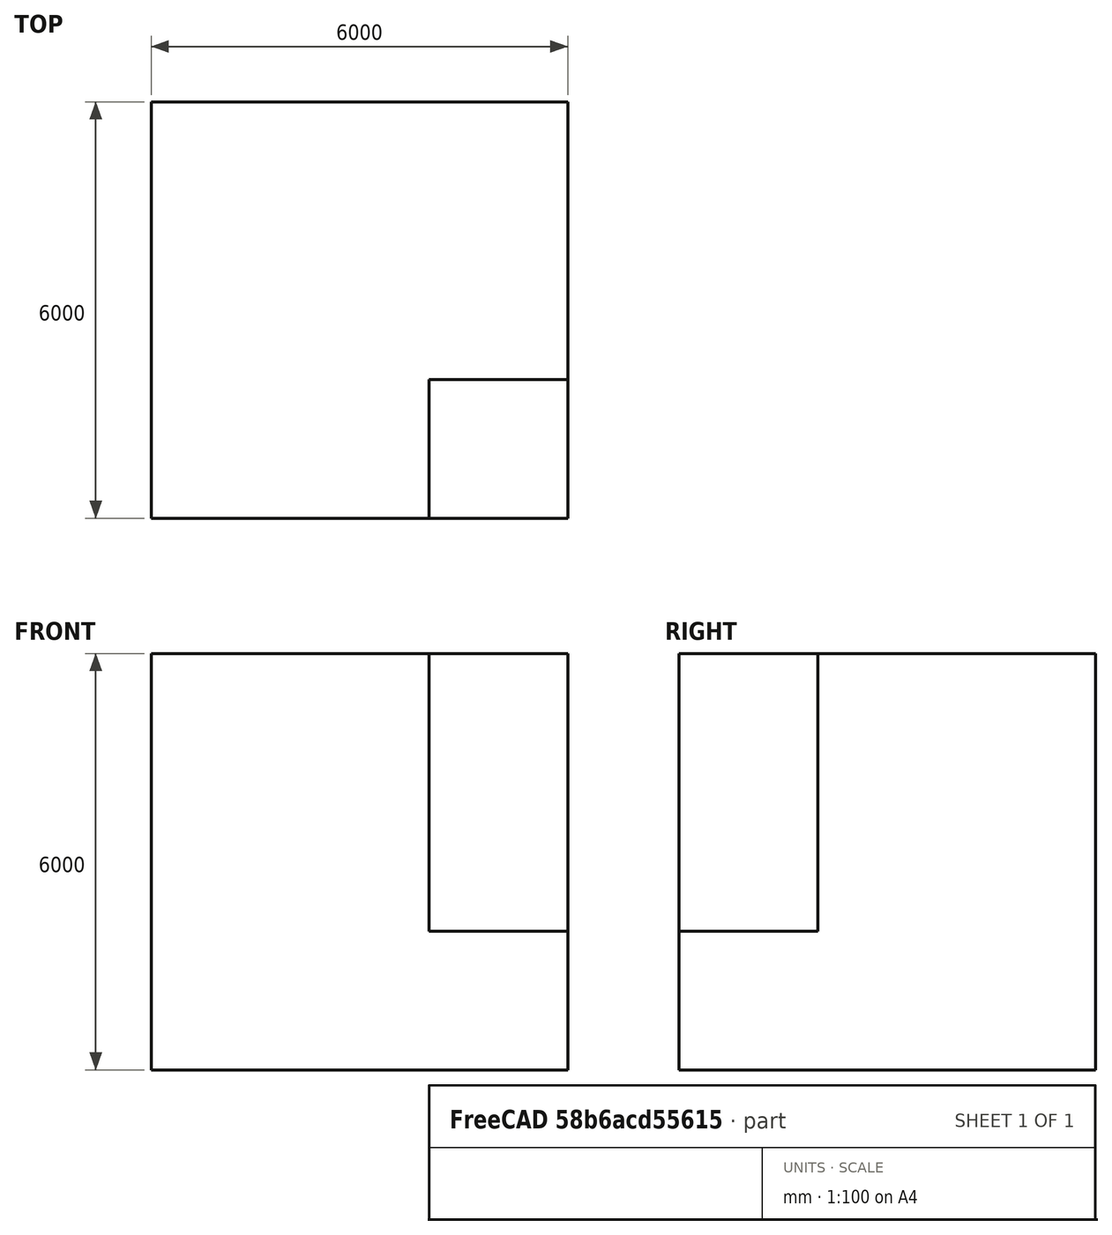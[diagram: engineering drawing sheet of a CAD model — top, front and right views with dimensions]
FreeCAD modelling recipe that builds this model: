
FCSTD DOCUMENT  (FreeCAD 0.21R33694 (Git))
Label: Pit_Example
License: All rights reserved
LicenseURL: http://en.wikipedia.org/wiki/All_rights_reserved
objects: Fem::ConstraintDisplacement×3, Part::Box×2, Fem::FemMeshObjectPython×2, Part::FeaturePython×1, App::MaterialObjectPython×1, Fem::FemSolverObjectPython×1, Fem::FemResultObjectPython×1, Fem::FemAnalysis×1
note: 3 computed .brp shape members not serialized (recipe doc carries the construction recipe); baked Part::Feature solids carry a one-line shape summary decoded from their .brp

FEATURE [Part::Box] Box  label="Cube"
  AttacherType = Attacher::AttachEngine3D
  Height = 6000
  Length = 6000
  Width = 6000
FEATURE [Part::Box] Box001  label="Cube001"
  AttacherType = Attacher::AttachEngine3D
  Height = 4000
  Length = 2000
  Placement = pos=(4000,0,2000) rot=(0,0,1;0rad)
  Width = 2000
FEATURE [Part::FeaturePython] XOR  # WARN: FeaturePython — macro-defined, semantics opaque (R4)
  Objects = -> [Box,Box001]
  Tolerance = 0
FEATURE [Fem::FemMeshObjectPython] FEMMeshGmsh  # FEM object (typed FeaturePython)
  Algorithm2D = 0
  Algorithm3D = 0
  CharacteristicLengthMax = 1000
  CharacteristicLengthMin = 1000
  CoherenceMesh = true
  ElementDimension = 0
  ElementOrder = 1
  GeometryTolerance = 1e-06
  GroupsOfNodes = false
  HighOrderOptimize = 0
  MeshSizeFromCurvature = 12
  OptimizeNetgen = false
  OptimizeStd = true
  Part = -> XOR
  RecombinationAlgorithm = 0
  Recombine3DAll = false
  RecombineAll = false
  SecondOrderLinear = false
FEATURE [Fem::ConstraintDisplacement] FemConstraintDisplacement
  NormalDirection = (0,-1,0)
  Normals = (82) [(0,-1,0),(0,-1,0),(0,-1,0),(0,-1,0),(0,-1,0),(0,-1,0),(0,-1,0),(0,-1,0),(0,-1,0),(0,-1,0),(0,-1,0),(0,-1,0),(0,-1,0),(0,-1,0),(0,-1,0),(0,-1,0),+66 more]
  Points = (82) [(0,0,0),(0,0,666.667),(0,0,1333.33),(0,0,2000),(0,0,2666.67),(0,0,3333.33),(0,0,4000),(0,0,4666.67),(0,0,5333.33),(0,0,6000),(666.667,0,0),+71 more]
  References = -> [XOR]
  Scale = 66
  hasXFormula = false
  hasYFormula = false
  hasZFormula = false
  rotxFix = false
  rotxFree = true
  rotyFix = false
  rotyFree = true
  rotzFix = false
  rotzFree = true
  useFlowSurfaceForce = false
  xDisplacement = 0
  xFix = false
  xFree = true
  xRotation = 0
  yDisplacement = 0
  yFix = true
  yFree = false
  yRotation = 0
  zDisplacement = 0
  zFix = false
  zFree = true
  zRotation = 0
FEATURE [Fem::ConstraintDisplacement] FemConstraintDisplacement001
  NormalDirection = (1,0,0)
  Normals = (82) [(1,0,0),(1,0,0),(1,0,0),(1,0,0),(1,0,0),(1,0,0),(1,0,0),(1,0,0),(1,0,0),(1,0,0),(1,0,0),(1,0,0),(1,0,0),(1,0,0),(1,0,0),(1,0,0),(1,0,0),(1,0,0),+64 more]
  Points = (82) [(6000,6000,0),(6000,6000,666.667),(6000,6000,1333.33),(6000,6000,2000),(6000,6000,2666.67),(6000,6000,3333.33),(6000,6000,4000),(6000,6000,4666.67),+74 more]
  References = -> [XOR]
  Scale = 66
  hasXFormula = false
  hasYFormula = false
  hasZFormula = false
  rotxFix = false
  rotxFree = true
  rotyFix = false
  rotyFree = true
  rotzFix = false
  rotzFree = true
  useFlowSurfaceForce = false
  xDisplacement = 0
  xFix = true
  xFree = false
  xRotation = 0
  yDisplacement = 0
  yFix = false
  yFree = true
  yRotation = 0
  zDisplacement = 0
  zFix = false
  zFree = true
  zRotation = 0
FEATURE [Fem::ConstraintDisplacement] FemConstraintDisplacement002
  NormalDirection = (-1,0,0)
  Normals = (300) [(-1,0,0),(-1,0,0),(-1,0,0),(-1,0,0),(-1,0,0),(-1,0,0),(-1,0,0),(-1,0,0),(-1,0,0),(-1,0,0),(-1,0,0),(-1,0,0),(-1,0,0),(-1,0,0),(-1,0,0),(-1,0,0),+284 more]
  Points = (300) [(0,6000,0),(0,6000,666.667),(0,6000,1333.33),(0,6000,2000),(0,6000,2666.67),(0,6000,3333.33),(0,6000,4000),(0,6000,4666.67),(0,6000,5333.33),+291 more]
  References = -> [XOR]
  Scale = 66
  hasXFormula = false
  hasYFormula = false
  hasZFormula = false
  rotxFix = false
  rotxFree = true
  rotyFix = false
  rotyFree = true
  rotzFix = false
  rotzFree = true
  useFlowSurfaceForce = false
  xDisplacement = 0
  xFix = true
  xFree = false
  xRotation = 0
  yDisplacement = 0
  yFix = true
  yFree = false
  yRotation = 0
  zDisplacement = 0
  zFix = true
  zFree = false
  zRotation = 0
FEATURE [App::MaterialObjectPython] SolidMaterial  # material (typed FeaturePython)
  Category = 0
  Material = Density=2000 kg/m^3,Description=Standard steel material for CalculiX sample calculations,Father=Metal,Name=CalculiX-Steel,PoissonRatio=0.3,+4 more (map truncated)
FEATURE [Fem::FemSolverObjectPython] SolverCcxTools  # FEM object (typed FeaturePython)
  AnalysisType = 0
  BeamShellResultOutput3D = false
  BucklingFactors = 1
  EigenmodeHighLimit = 1000000
  EigenmodeLowLimit = 0
  EigenmodesCount = 10
  GeometricalNonlinearity = 0
  IterationsControlParameterCutb = 0.25,0.5,0.75,0.85,,,1.5,
  IterationsControlParameterIter = 4,8,9,200,10,400,,200,,
  IterationsControlParameterTimeUse = false
  IterationsThermoMechMaximum = 2000
  IterationsUserDefinedIncrementations = false
  IterationsUserDefinedTimeStepLength = false
  MaterialNonlinearity = 0
  MatrixSolverType = 0
  SplitInputWriter = false
  ThermoMechSteadyState = true
  TimeEnd = 1
  TimeInitialStep = 0.01
FEATURE [Fem::FemMeshObjectPython] Result_Mesh_Volume  # FEM object (typed FeaturePython)
FEATURE [Fem::FemResultObjectPython] ResultMechanical  # FEM object (typed FeaturePython)
  CriticalStrainRatio = [3.93271e-11,3.65733e-15,3.60697e-13,0,1.03974e-16,0,5.69735e-13,0,2.90723e-11,0,4.77787e-14,3.35108e-15,3.15501e-13,5.30155e-13,1.25867e-14,3.70262e-14,9.67589e-14,1.55294e-13,4.09489e-13,6.47917e-15,2.40662e-14,5.35308e-14,1.18882e-13,+2136 more]
  DisplacementLengths = [0,0,0,0,0,13.4161,499.853,1214.43,0,1229.44,1042.92,0,395.681,315.697,0,0,0,0,0,0,0,0,0,0,0,0,0,0,0,0,0,0,0,0,0,0,0,0,0,0,0,0,0,0,0,0,0,0,0,0,0,0,0,0,0,0,0,0,26.8115,21.3072,22.4792,44.2649,244.595,20.9739,1203.36,1133.48,1185.39,1077,+2091 more]
  DisplacementVectors = (2159) [(0,0,0),(0,0,0),(0,0,0),(0,0,0),(0,0,0),(0,0,-13.4161),(471.161,0,-166.914),(359.54,0,-1159.99),(0,0,0),(0,-364.791,-1174.08),+2149 more]
  Eigenmode = 0
  EigenmodeFrequency = 0
  MaxShear = [0.0120873,0.00838715,0.00834008,0.00200348,0.0119649,0.0107051,0.0124848,0.00878505,0.0122617,0.00891737,0.00945304,0.0083381,0.0122458,0.0106498,0.0122897,0.0124146,0.0123189,0.0117055,0.0119133,0.0123287,0.0116299,0.0122706,0.0117304,+2136 more]
  Mesh = -> Result_Mesh_Volume
  NodeNumbers = [1,2,3,4,5,6,7,8,9,10,11,12,13,14,15,16,17,18,19,20,21,22,23,24,25,26,27,28,29,30,31,32,33,34,35,36,37,38,39,40,41,42,43,44,45,46,47,48,49,50,51,52,53,54,55,56,57,58,59,60,61,62,63,64,65,66,67,68,69,+2090 more]
  NodeStressXX = [0.0426116,-0.0287495,0.0225941,0.000184001,-0.0236186,-0.0213899,-0.0258921,-0.000334487,0.0374222,-0.0176534,-0.0194084,-0.0200504,-0.0263269,-0.0342568,-0.0468423,-0.0339447,-0.0240208,-0.0144466,-0.00358832,-0.0455244,-0.0404945,+2138 more]
  NodeStressXY = [0.000436366,0.00123217,-0.00346757,0.00119999,-0.000608948,0.000394579,-0.00115889,0.000984407,0.000109046,0.000807043,-0.00663616,0.00119992,-0.000516293,-0.00632209,4.25731e-05,-4.16024e-05,-7.06763e-06,-1.05395e-06,-1.28247e-05,+2140 more]
  NodeStressXZ = [-0.0114819,-0.00827964,-0.00392951,-0.0013586,0.00153304,8.95455e-05,0.0118325,0.000849509,-0.000294895,0.000139663,1.71635e-05,-0.00121717,-0.0016558,0.00682086,-0.0110895,-0.0121039,-0.0121837,-0.0116967,-0.0118399,-0.0101755,-0.0110692,+2138 more]
  NodeStressYY = [0.0416871,-0.0204887,0.0222457,9.08532e-05,-0.0239155,-0.0208947,-0.0282729,-0.0170663,0.0379403,-0.000990802,-0.0198669,-0.0277336,-0.0258271,-0.0339999,-0.0380442,-0.0296529,-0.0212854,-0.0135228,-0.0012541,-0.0331274,-0.0339659,+2138 more]
  NodeStressYZ = [0.000121712,0.00118817,0.00397418,0.00141301,-0.0015193,-0.000209556,0.00261372,-0.00023663,0.0118684,-0.00119348,1.03204e-06,0.00821444,-0.012117,-0.00570276,-5.44293e-05,-0.000192069,-9.10624e-05,3.38103e-06,3.55138e-05,-7.92996e-05,+2139 more]
  NodeStressZZ = [0.0351114,-0.0284917,0.0135113,-0.000274854,-0.0466795,-0.000201879,-0.0316048,-0.000532762,0.031807,-0.00114916,-0.00737171,-0.0285296,-0.0265316,-0.0393612,-0.0362493,-0.0284385,-0.0203857,-0.0135372,-0.000947366,-0.0316035,-0.0333606,+2138 more]
  Peeq = [0.951469,0.0391219,0.0579614,0,0.00164483,0,1.9534,0,0.933438,0,0.320892,0.0372375,2.29672,1.95049,0.122964,0.209744,0.318828,0.414748,0.525644,0.0689533,0.166354,0.251684,0.366721,0.469654,0.59357,1.10874,0.783864,0.503741,0.526748,+2130 more]
  PrincipalMax = [0.0509488,-0.0203035,0.0280402,0.00133833,-0.0229462,-0.000199412,-0.0165324,0.000441177,0.0471328,0.000139962,-0.00737168,-0.0198567,-0.0140071,-0.0230062,-0.0292558,-0.0187771,-0.00988433,-0.00228638,0.00964555,-0.0262351,-0.0252978,+2138 more]
  PrincipalMed = [0.0416869,-0.0203485,0.0189509,0.00133029,-0.0243915,-0.0206774,-0.0277355,-0.00124577,0.0374273,-0.00223857,-0.0129975,-0.0199241,-0.0261799,-0.0403059,-0.0380447,-0.0296526,-0.0212854,-0.0135228,-0.0012542,-0.0331277,-0.0339657,+2138 more]
  PrincipalMin = [0.0267743,-0.0370778,0.01136,-0.00266863,-0.0468759,-0.0216096,-0.041502,-0.0171289,0.0226094,-0.0176948,-0.0262778,-0.0365329,-0.0384986,-0.0443058,-0.0538353,-0.0436063,-0.0345221,-0.0256975,-0.0141811,-0.0508925,-0.0485575,-0.0384965,+2137 more]
  ResultType = Fem::ResultMechanical
  Stats = [-64.9146,1006.1,-1031.26,67.7725,-1174.08,125.506,0,1233.76,1.68227e-17,0.0269422,-0.0600846,0.0814701,-0.0611045,0.0682511,-0.080742,0.055561,9.12772e-18,0.0149205,0,2.44517,0,3.93271e-11,0,0,0,0]
  Temperature = [3.93271e-11,3.65733e-15,3.60697e-13,0,1.03974e-16,0,5.69735e-13,0,2.90723e-11,0,4.77787e-14,3.35108e-15,3.15501e-13,5.30155e-13,1.25867e-14,3.70262e-14,9.67589e-14,1.55294e-13,4.09489e-13,6.47917e-15,2.40662e-14,5.35308e-14,1.18882e-13,+2136 more]
  Time = 0
  vonMises = [0.0211256,0.0167518,0.0144649,0.00400294,0.0232408,0.0209597,0.0216622,0.0167903,0.0213912,0.0167724,0.0168145,0.0166426,0.0212104,0.019608,0.0215724,0.0215578,0.0213567,0.02028,0.0206594,0.022035,0.0203601,0.021291,0.0203384,0.0203079,+2135 more]
FEATURE [Fem::FemAnalysis] Analysis
  Group = -> [FEMMeshGmsh,FemConstraintDisplacement,FemConstraintDisplacement001,FemConstraintDisplacement002,SolidMaterial,SolverCcxTools,ResultMechanical]
